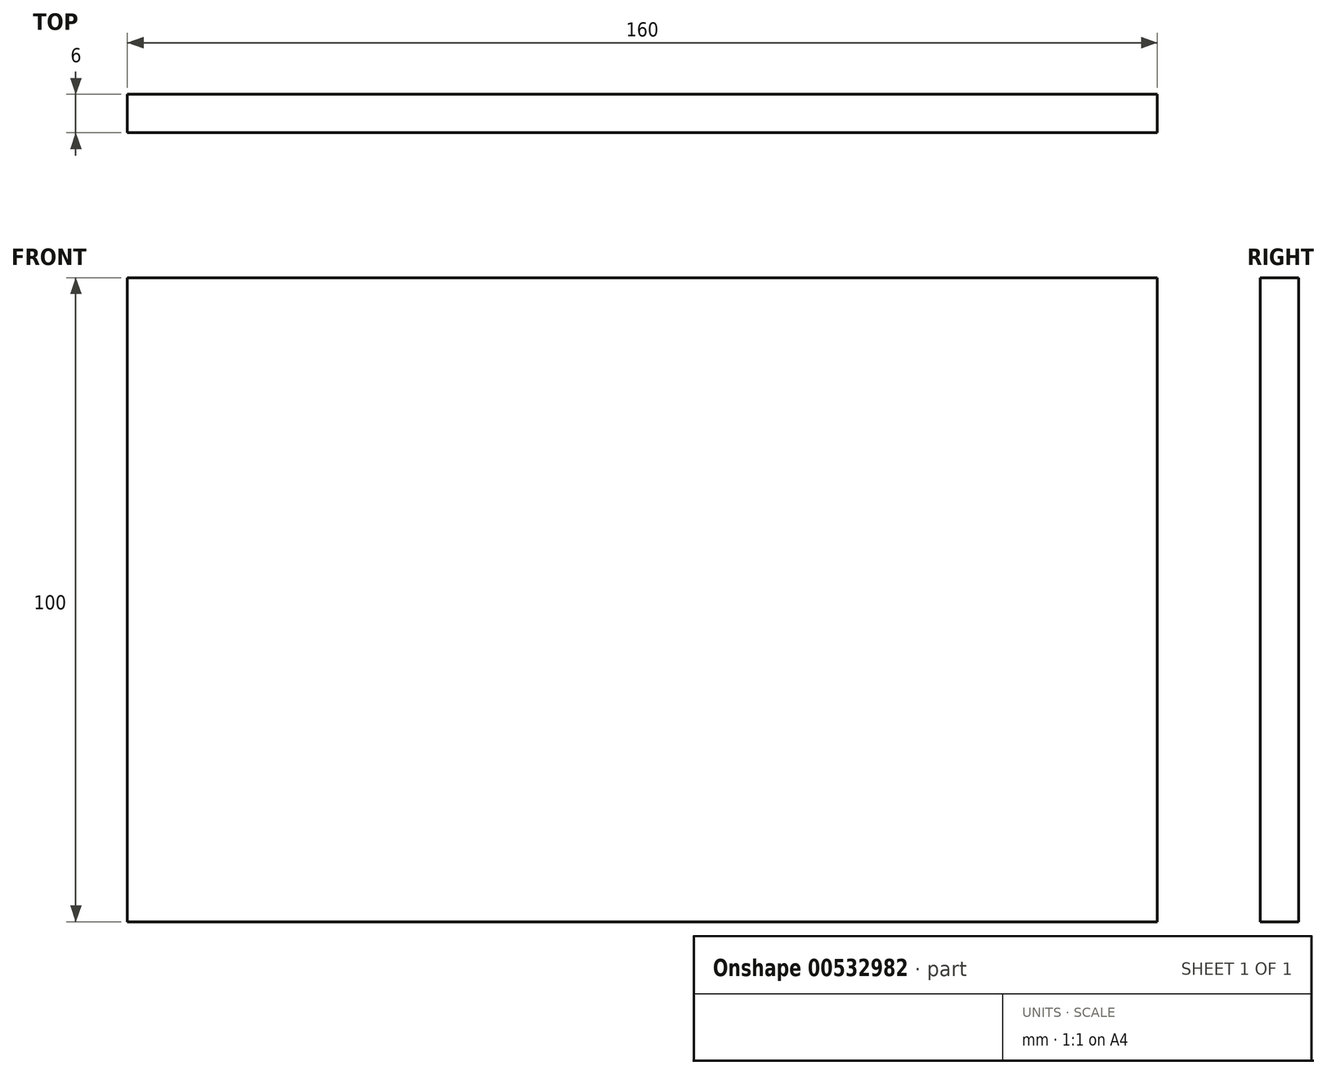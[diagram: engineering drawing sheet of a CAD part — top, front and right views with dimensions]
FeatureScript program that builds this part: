
annotation { "Feature Type Name" : "Feature", "Feature Type Description" : "" }
export const myFeature = defineFeature(function(context is Context, id is Id, definition is map)
    precondition{}
    {
        {
            var Q0;
            Q0=qCreatedBy(makeId("Front.planeOp"),FACE);
            var sketch = newSketch(context, id + "F0", { "sketchPlane" : qUnion([Q0])});
            skLineSegment(sketch, "E0.bottom", {"start": v(-107.15, 58.14) * mm, "end": v(52.85, 58.14) * mm});
            skLineSegment(sketch, "E0.top", {"start": v(-107.15, -41.86) * mm, "end": v(52.85, -41.86) * mm});
            skLineSegment(sketch, "E0.left", {"start": v(-107.15, 58.14) * mm, "end": v(-107.15, -41.86) * mm});
            skLineSegment(sketch, "E0.right", {"start": v(52.85, 58.14) * mm, "end": v(52.85, -41.86) * mm});
            skSolve(sketch);
        }
        {
            var Q0;
            Q0 = qSketchRegion(id + "F0", true);
            var Q1;
            Q1=makeQuery(id+"F0.imprint","IMPRINT",FACE,{"disambiguationData":[TD([[makeQuery(id+"F0.imprint","IMPRINT",EDGE,{"derivedFrom":sQuery(id+"F0.wireOp",EDGE,"E0.bottom")}),-1.0]])]});
            extrude(context, id + "F1", {"entities" : qUnion([Q0, Q1]), "depth" : 6 * mm, "offsetDistance" : 25 * mm});
        }
    });
